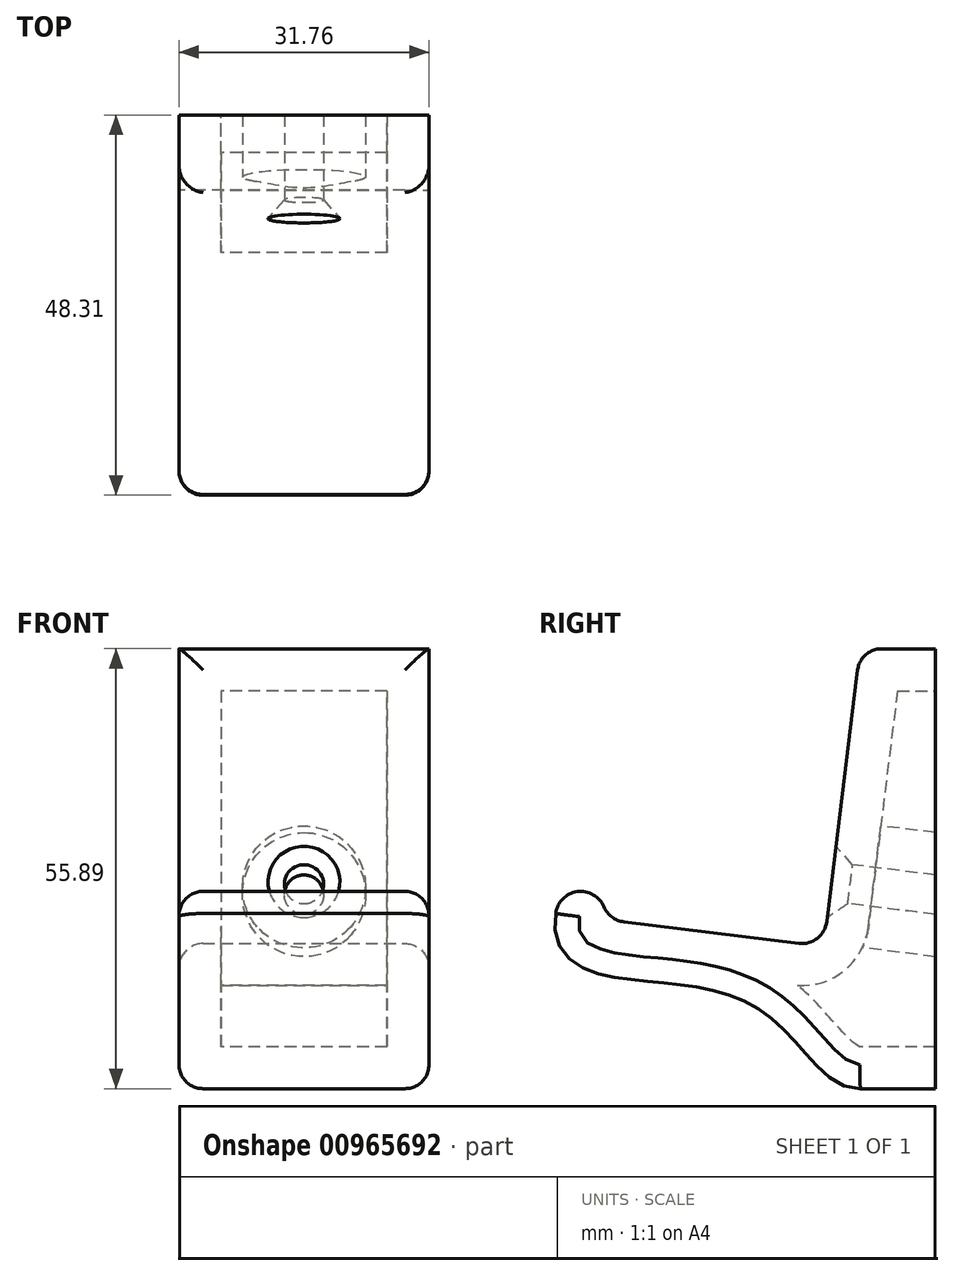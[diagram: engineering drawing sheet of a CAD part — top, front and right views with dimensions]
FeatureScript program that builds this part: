
annotation { "Feature Type Name" : "Feature", "Feature Type Description" : "" }
export const myFeature = defineFeature(function(context is Context, id is Id, definition is map)
    precondition{}
    {
        {
            var Q0;
            Q0=qCreatedBy(makeId("Right.planeOp"),FACE);
            var sketch = newSketch(context, id + "F0", { "sketchPlane" : qUnion([Q0])});
            skLineSegment(sketch, "E0", {"start": v(0, 0) * mm, "end": v(0, 37.82) * mm});
            skLineSegment(sketch, "E1", {"start": v(0, 37.82) * mm, "end": v(-4.64, 0) * mm});
            skLineSegment(sketch, "E2", {"start": v(-4.64, 0) * mm, "end": v(0, 0) * mm});
            skLineSegment(sketch, "E3.bottom", {"start": v(0, 37.82) * mm, "end": v(9.52, 37.82) * mm});
            skLineSegment(sketch, "E3.top", {"start": v(0, -18.06) * mm, "end": v(9.53, -18.06) * mm});
            skLineSegment(sketch, "E3.left", {"start": v(0, 37.82) * mm, "end": v(0, -18.06) * mm});
            skLineSegment(sketch, "E3.right", {"start": v(9.52, 37.82) * mm, "end": v(9.53, -18.06) * mm});
            skLineSegment(sketch, "E4", {"start": v(-4.64, 0) * mm, "end": v(-38.68, 4.18) * mm});
            skFitSpline(sketch, "E5", {"points": [v(-38.68, 4.18) * mm, v(-24.66, -4.65) * mm, v(-10.46, -9.84) * mm, v(0, -18.06) * mm], "startDerivative": vector(-9.65, -69.18) * mm, "endDerivative": vector(38.8, 1.58) * mm});
            skArc(sketch, "E6", {"start": v(-32.33, 3.4) * mm, "mid": v(-35.11, 6.96) * mm, "end": v(-38.68, 4.18) * mm});
            skSolve(sketch);
        }
        {
            var Q0;
            {var subQ0=sQuery(id+"F0.wireOp",EDGE,"E1");Q0=makeQuery(id+"F0.imprint","IMPRINT",FACE,{"disambiguationData":[TD([[makeQuery(id+"F0.imprint","IMPRINT",EDGE,{"derivedFrom":subQ0}),1.0]])]});}
            var Q1;
            {var subQ4=sQuery(id+"F0.wireOp",EDGE,"E2");Q1=makeQuery(id+"F0.imprint","IMPRINT",FACE,{"disambiguationData":[TD([[makeQuery(id+"F0.imprint","IMPRINT",EDGE,{"derivedFrom":subQ4}),-1.0]])]});}
            var Q2;
            {var subQ0=sQuery(id+"F0.wireOp",EDGE,"E6");Q2=makeQuery(id+"F0.imprint","IMPRINT",FACE,{"disambiguationData":[TD([[makeQuery(id+"F0.imprint","IMPRINT",EDGE,{"derivedFrom":subQ0}),1.0]])]});}
            extrude(context, id + "F1", {"entities" : qUnion([Q0, Q1, Q2]), "endBound" : BoundingType.SYMMETRIC, "depth" : 31.75 * mm, "offsetDistance" : 25.4 * mm});
        }
        {
            var Q0;
            Q0=makeQuery(id+"F1.opExtrude","SWEPT_EDGE",EDGE,{"disambiguationData":[OSD([sQuery(id+"F0.wireOp",EDGE,"E1"),sQuery(id+"F0.wireOp",EDGE,"E2"),sQuery(id+"F0.wireOp",EDGE,"E4")])]});
            var Q1;
            Q1=makeQuery(id+"F1.opExtrude","SWEPT_EDGE",EDGE,{"disambiguationData":[OSD([sQuery(id+"F0.wireOp",EDGE,"E4"),sQuery(id+"F0.wireOp",EDGE,"E6")])]});
            fillet(context, id + "F2", {"entities" : qUnion([Q0, Q1]), "radius" : 3.17 * mm, "tangentPropagation" : true, "allowEdgeOverflow" : false});
        }
        {
            var Q0;
            Q0 = qSketchRegion(id + "F0", true);
            extrude(context, id + "F3", {"entities" : qUnion([Q0]), "operationType" : NewBodyOperationType.ADD, "endBound" : BoundingType.SYMMETRIC, "depth" : 31.75 * mm, "offsetDistance" : 25.4 * mm});
        }
        {
            var Q0;
            Q0=makeQuery(id+"F1.opExtrude","SWEPT_FACE",FACE,{"disambiguationData":[OSD([sQuery(id+"F0.wireOp",EDGE,"E1")])]});
            var sketch = newSketch(context, id + "F4", { "sketchPlane" : qUnion([Q0])});
            skPoint(sketch, "E7", {"position": v(0, 7.69) * mm});
            skPoint(sketch, "E7.positionSnap0", {"position": v(0, 2.6) * mm});
            skSolve(sketch);
        }
        {
            var Q0;
            Q0=sQuery(id+"F4.wireOp",VERTEX,"E7");
            var Q1;
            Q1=makeQuery(id+"F1.opExtrude","SWEPT_BODY",BODY,{"disambiguationData":[OSD([sQuery(id+"F0.wireOp",EDGE,"E1"),sQuery(id+"F0.wireOp",EDGE,"E3.left"),sQuery(id+"F0.wireOp",EDGE,"E4"),sQuery(id+"F0.wireOp",EDGE,"E5"),sQuery(id+"F0.wireOp",EDGE,"E6")])]});
            hole(context, id + "F5", {"style" : HoleStyle.C_SINK, "endStyle" : HoleEndStyle.THROUGH, "standardTappedOrClearance" : lookupTablePath({ "fit" : "Normal (ASME)", "standard" : "ANSI", "size" : "#8", "type" : "Clearance" }), "standardBlindInLast" : lookupTablePath({ "fit" : "Normal", "standard" : "ANSI", "engagement" : "75%", "pitch" : "32 tpi", "size" : "#8", "type" : "Clearance & tapped" }), "holeDiameter" : 4.98 * mm, "cSinkDiameter" : 9.12 * mm, "cSinkAngle" : 82 * degree, "majorDiameter" : 6.35 * mm, "isTappedThrough" : true, "tappedDepth" : 12.7 * mm, "tapClearance" : 3, "locations" : qUnion([Q0]), "scope" : qUnion([Q1])});
        }
        {
            var Q0;
            Q0=makeQuery(id+"F1.opExtrude","CAP_EDGE",EDGE,{"disambiguationData":[OSD([sQuery(id+"F0.wireOp",EDGE,"E5")])],"isStart":true});
            var Q1;
            Q1=makeQuery(id+"F1.opExtrude","CAP_EDGE",EDGE,{"disambiguationData":[OSD([sQuery(id+"F0.wireOp",EDGE,"E4")])],"isStart":true});
            var Q2;
            {var subQ0=sQuery(id+"F0.wireOp",EDGE,"E6");var subQ1=sQuery(id+"F0.wireOp",EDGE,"E4");Q2=makeQuery(id+"F2.opFillet","BLEND_EDGE",EDGE,{"blendedFrom":[makeQuery(id+"F1.opExtrude","SWEPT_EDGE",EDGE,{"disambiguationData":[OSD([subQ1,subQ0])]}),makeQuery(id+"F1.opExtrude","CAP_FACE",FACE,{"disambiguationData":[OSD([sQuery(id+"F0.wireOp",EDGE,"E1"),sQuery(id+"F0.wireOp",EDGE,"E3.left"),subQ1,sQuery(id+"F0.wireOp",EDGE,"E5"),subQ0])],"isStart":true})],"blendedInto":[makeQuery(id+"F1.opExtrude","CAP_FACE",FACE,{"disambiguationData":[OSD([sQuery(id+"F0.wireOp",EDGE,"E1"),sQuery(id+"F0.wireOp",EDGE,"E3.left"),subQ1,sQuery(id+"F0.wireOp",EDGE,"E5"),subQ0])],"isStart":true})]});}
            var Q3;
            Q3=makeQuery(id+"F1.opExtrude","CAP_EDGE",EDGE,{"disambiguationData":[OSD([sQuery(id+"F0.wireOp",EDGE,"E6")])],"isStart":true});
            var Q4;
            {var subQ0=sQuery(id+"F0.wireOp",EDGE,"E4");var subQ1=sQuery(id+"F0.wireOp",EDGE,"E1");Q4=makeQuery(id+"F2.opFillet","BLEND_EDGE",EDGE,{"blendedFrom":[makeQuery(id+"F1.opExtrude","SWEPT_EDGE",EDGE,{"disambiguationData":[OSD([subQ1,sQuery(id+"F0.wireOp",EDGE,"E2"),subQ0])]}),makeQuery(id+"F1.opExtrude","CAP_FACE",FACE,{"disambiguationData":[OSD([subQ1,sQuery(id+"F0.wireOp",EDGE,"E3.left"),subQ0,sQuery(id+"F0.wireOp",EDGE,"E5"),sQuery(id+"F0.wireOp",EDGE,"E6")])],"isStart":true})],"blendedInto":[makeQuery(id+"F1.opExtrude","CAP_FACE",FACE,{"disambiguationData":[OSD([subQ1,sQuery(id+"F0.wireOp",EDGE,"E3.left"),subQ0,sQuery(id+"F0.wireOp",EDGE,"E5"),sQuery(id+"F0.wireOp",EDGE,"E6")])],"isStart":true})]});}
            var Q5;
            Q5=makeQuery(id+"F1.opExtrude","CAP_EDGE",EDGE,{"disambiguationData":[OSD([sQuery(id+"F0.wireOp",EDGE,"E1")])],"isStart":true});
            var Q6;
            {var subQ0=sQuery(id+"F0.wireOp",EDGE,"E3.left");var subQ1=sQuery(id+"F0.wireOp",EDGE,"E3.bottom");var subQ2=sQuery(id+"F0.wireOp",EDGE,"E1");Q6=makeQuery(id+"F3.boolean.opBoolean","MERGE",EDGE,{"derivedFrom":[makeQuery(id+"F1.opExtrude","SWEPT_EDGE",EDGE,{"disambiguationData":[OSD([subQ2,subQ1,subQ0])]}),makeQuery(id+"F3.opExtrude","SWEPT_EDGE",EDGE,{"disambiguationData":[OSD([subQ2,subQ1,subQ0])]})]});}
            var Q7;
            Q7=makeQuery(id+"F1.opExtrude","CAP_EDGE",EDGE,{"disambiguationData":[OSD([sQuery(id+"F0.wireOp",EDGE,"E1")])],"isStart":false});
            fillet(context, id + "F6", {"entities" : qUnion([Q0, Q1, Q2, Q3, Q4, Q5, Q6, Q7]), "radius" : 3.05 * mm, "tangentPropagation" : true, "allowEdgeOverflow" : false});
        }
        {
            var Q0;
            Q0=makeQuery(id+"F3.opExtrude","SWEPT_FACE",FACE,{"disambiguationData":[OSD([sQuery(id+"F0.wireOp",EDGE,"E3.right")])]});
            shell(context, id + "F7", {"entities" : qUnion([Q0]), "thickness" : 5.33 * mm});
        }
    });
